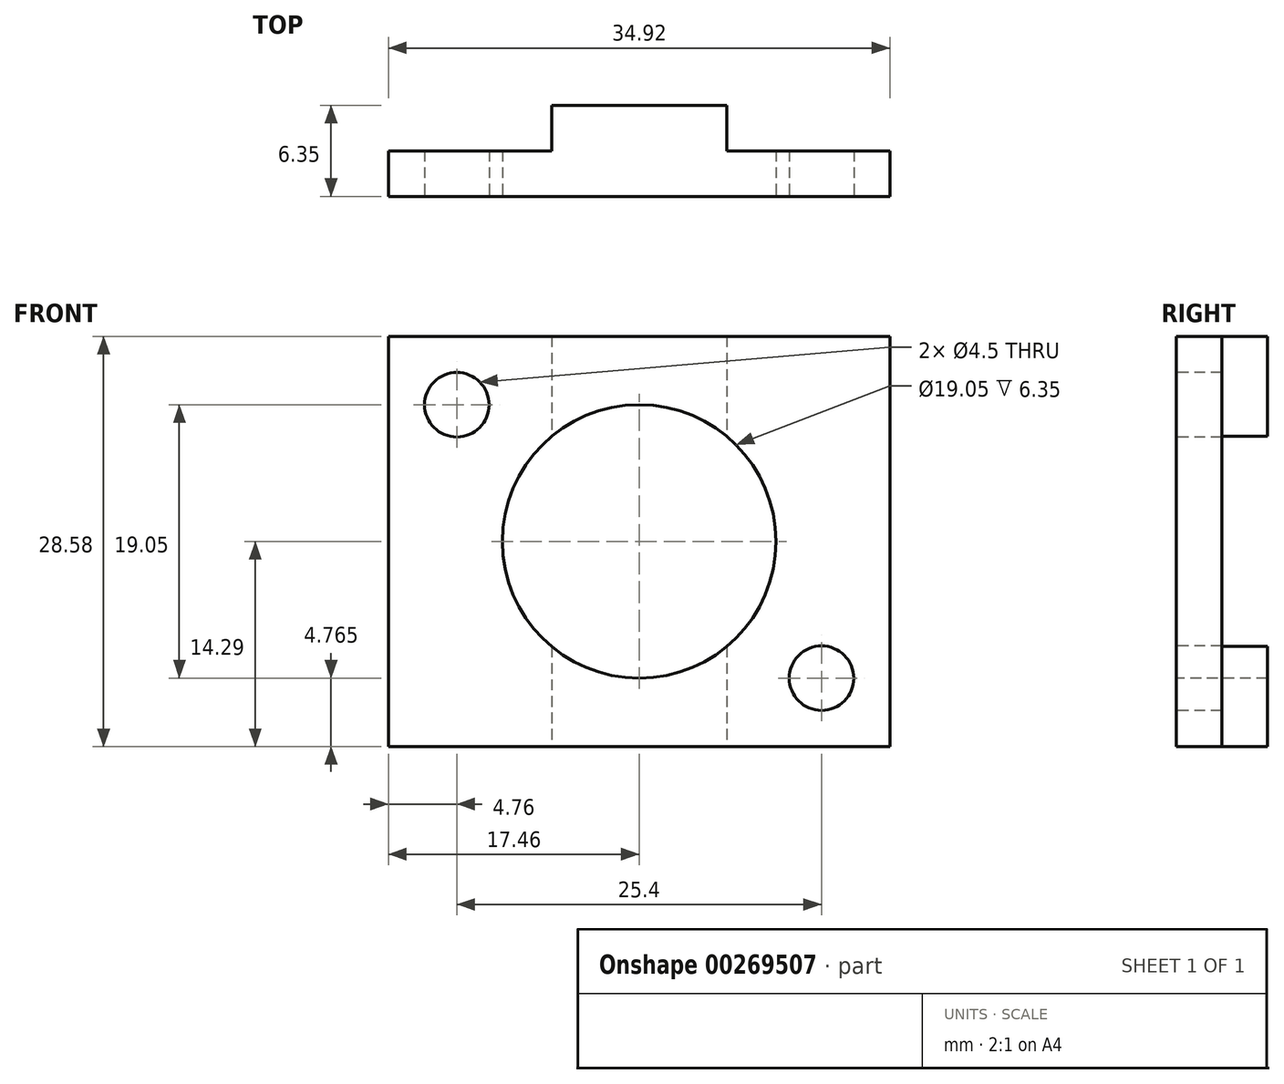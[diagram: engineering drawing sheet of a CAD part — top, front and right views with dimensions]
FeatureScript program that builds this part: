
annotation { "Feature Type Name" : "Feature", "Feature Type Description" : "" }
export const myFeature = defineFeature(function(context is Context, id is Id, definition is map)
    precondition{}
    {
        {
            var Q0;
            Q0=qCreatedBy(makeId("Front.planeOp"),FACE);
            var sketch = newSketch(context, id + "F0", { "sketchPlane" : qUnion([Q0])});
            skLineSegment(sketch, "E0.bottom", {"start": v(17.46, -14.29) * mm, "end": v(-17.46, -14.29) * mm});
            skLineSegment(sketch, "E0.top", {"start": v(17.46, 14.29) * mm, "end": v(-17.46, 14.29) * mm});
            skLineSegment(sketch, "E0.left", {"start": v(17.46, -14.29) * mm, "end": v(17.46, 14.29) * mm});
            skLineSegment(sketch, "E0.right", {"start": v(-17.46, -14.29) * mm, "end": v(-17.46, 14.29) * mm});
            skPoint(sketch, "E0.middle", {"position": v(0, 0) * mm});
            skSolve(sketch);
        }
        {
            var Q0;
            Q0 = qSketchRegion(id + "F0", true);
            extrude(context, id + "F1", {"entities" : qUnion([Q0]), "endBound" : BoundingType.SYMMETRIC, "depth" : 3.17 * mm});
        }
        {
            var Q0;
            Q0=makeQuery(id+"F1.opExtrude","CAP_FACE",FACE,{"disambiguationData":[OSD([sQuery(id+"F0.wireOp",EDGE,"E0.bottom"),sQuery(id+"F0.wireOp",EDGE,"E0.top"),sQuery(id+"F0.wireOp",EDGE,"E0.left"),sQuery(id+"F0.wireOp",EDGE,"E0.right")])],"isStart":false});
            var sketch = newSketch(context, id + "F2", { "sketchPlane" : qUnion([Q0])});
            skLineSegment(sketch, "E1.bottom", {"start": v(12.7, 9.53) * mm, "end": v(-12.7, 9.53) * mm});
            skLineSegment(sketch, "E1.top", {"start": v(12.7, -9.53) * mm, "end": v(-12.7, -9.53) * mm});
            skLineSegment(sketch, "E1.left", {"start": v(12.7, 9.53) * mm, "end": v(12.7, -9.53) * mm});
            skLineSegment(sketch, "E1.right", {"start": v(-12.7, 9.53) * mm, "end": v(-12.7, -9.53) * mm});
            skPoint(sketch, "E1.middle", {"position": v(0, 0) * mm});
            skSolve(sketch);
        }
        {
            var Q0;
            Q0=sQuery(id+"F2.wireOp",VERTEX,"E1.right.start");
            var Q1;
            Q1=sQuery(id+"F2.wireOp",VERTEX,"E1.left.end");
            var Q2;
            Q2=makeQuery(id+"F1.opExtrude","SWEPT_BODY",BODY,{"disambiguationData":[OSD([sQuery(id+"F0.wireOp",EDGE,"E0.bottom"),sQuery(id+"F0.wireOp",EDGE,"E0.top"),sQuery(id+"F0.wireOp",EDGE,"E0.left"),sQuery(id+"F0.wireOp",EDGE,"E0.right")])]});
            hole(context, id + "F3", {"style" : HoleStyle.SIMPLE, "endStyle" : HoleEndStyle.BLIND, "standardTappedOrClearance" : lookupTablePath({ "standard" : "ANSI", "fit" : "Normal (ASME)", "size" : "#8", "type" : "Clearance" }), "standardBlindInLast" : lookupTablePath({ "fit" : "Free", "standard" : "ANSI", "size" : "#8", "type" : "Clearance" }), "holeDiameter" : 4.5 * mm, "holeDepth" : 12.7 * mm, "tappedDepth" : 10.32 * mm, "tapClearance" : 3, "locations" : qUnion([Q0, Q1]), "scope" : qUnion([Q2])});
        }
        {
            var Q0;
            Q0=makeQuery(id+"F1.opExtrude","CAP_FACE",FACE,{"disambiguationData":[OSD([sQuery(id+"F0.wireOp",EDGE,"E0.bottom"),sQuery(id+"F0.wireOp",EDGE,"E0.top"),sQuery(id+"F0.wireOp",EDGE,"E0.left"),sQuery(id+"F0.wireOp",EDGE,"E0.right")])],"isStart":true});
            var sketch = newSketch(context, id + "F4", { "sketchPlane" : qUnion([Q0])});
            skLineSegment(sketch, "E2.bottom", {"start": v(6.1, 14.29) * mm, "end": v(-6.1, 14.29) * mm});
            skLineSegment(sketch, "E2.top", {"start": v(6.1, -14.29) * mm, "end": v(-6.1, -14.29) * mm});
            skLineSegment(sketch, "E2.left", {"start": v(6.1, 14.29) * mm, "end": v(6.1, -14.29) * mm});
            skLineSegment(sketch, "E2.right", {"start": v(-6.1, 14.29) * mm, "end": v(-6.1, -14.29) * mm});
            skPoint(sketch, "E2.middle", {"position": v(0, 0) * mm});
            skSolve(sketch);
        }
        {
            var Q0;
            Q0 = qSketchRegion(id + "F4", true);
            extrude(context, id + "F5", {"entities" : qUnion([Q0]), "operationType" : NewBodyOperationType.ADD, "depth" : 3.17 * mm});
        }
        {
            var Q0;
            Q0=makeQuery(id+"F1.opExtrude","CAP_FACE",FACE,{"disambiguationData":[OSD([sQuery(id+"F0.wireOp",EDGE,"E0.bottom"),sQuery(id+"F0.wireOp",EDGE,"E0.top"),sQuery(id+"F0.wireOp",EDGE,"E0.left"),sQuery(id+"F0.wireOp",EDGE,"E0.right")])],"isStart":false});
            var sketch = newSketch(context, id + "F6", { "sketchPlane" : qUnion([Q0])});
            skCircle(sketch, "E3", {"center": v(0, 0) * mm, "radius": 9.53 * mm});
            skSolve(sketch);
        }
        {
            var Q0;
            Q0 = qSketchRegion(id + "F6", true);
            extrude(context, id + "F7", {"entities" : qUnion([Q0]), "operationType" : NewBodyOperationType.REMOVE, "endBound" : BoundingType.THROUGH_ALL, "oppositeDirection" : true, "depth" : 25.4 * mm});
        }
    });
